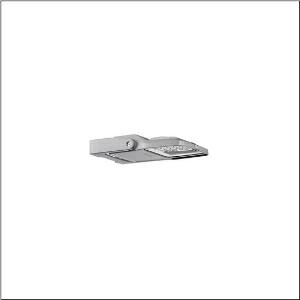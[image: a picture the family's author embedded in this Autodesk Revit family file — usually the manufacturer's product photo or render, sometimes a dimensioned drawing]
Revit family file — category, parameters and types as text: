
# Revit family: floodlight_fl_21_iq_micro___pl52_5xa7762a2d2a_5d06
name_source: partatom
category: Lighting Fixtures
units: mm (PartAtom-declared; Revit-internal decimal feet)

## family parameters
Cut with Voids When Loaded = No
Host = Face
Light Source = No
Part Type = Normal
Room Calculation Point = No
Round Connector Dimension = Use Diameter
Shared = No

## types (1)
- --- (1 x LED, 2890 lm, 23.1 W, 3000K)
    Apparent Load = 23 VA
    CIE Flux Codes = 26 60 98 100 100
    Color Rendering = 70
    Color Temperature = 3000K
    Default Elevation = 1800 mm
    Description = Floodlight FL 21 iQ micro, floodlight, primary light control with lens, of PMMA, primary optical cover: protective disc, of toughened safety glass, transparent, light distribution: PL52, light emission: direct distribution, installation type: surface-mounted, LED, High Power LED, rated luminous flux: 2.890lm, luminous efficacy: 125lm/W, light colour: 730, colour temperature: 3000K, control: Auto-Match, Temp-Guard, Night-Set, Smart-Wire, Desk-Remote (wireless, voltage-free reading and setting of iQ features in the workshop via application-optimized NFC function/RFID function), optimised constant luminous flux control (CLO 2.0), Street-Remote, with terminal, 6-pole, mains connection: 220..240V, AC, 50/60Hz, start of lifetime: 23W, end of service life: 24W, reduction: 11W, luminaire housing, of diecast aluminium, powder-coated, Siteco® metallic grey (DB 702S), corrosivity category C5 mid according to DIN EN ISO 12944, sealing non-destructively replaceable, design bracket, of diecast aluminium, powder-coated, Siteco® metallic grey (DB 702S), protection rating (complete): IP66, insulation class (complete): insulation class II (safety insulation), certification: CE, ENEC, VDE, protection symbol: D, impact resistance: IK07, permissible operating ambient temperature: -40..+40°C, permissible operating ambient temperature for outdoor applications: -40..+50°C, standard: DIN EN 12944, LABS conformity tested according to VDMA 24364:2018-05, packaging unit: 1 piece

Light Distribution: PL52
    Height = 65 mm
    Lamp = 1 x LED
    Lamp Light Flux = 2890 lm
    Lamp Power = 23.1 W
    Lamp count = 1
    Length = 312 mm
    Luminous efficacy = 125 lm/W
    Manufacturer = Siteco
    ModVariant = No
    Model = 5XA7762A2D2A
    Mounting Place = Wall
    Mounting Type = Surface mounted
    Number of Poles = 1
    OnlyDefault = Yes
    Power Factor = 1
    Product Name = Floodlight FL 21 iQ micro | PL52
    Product group = floodlight | wall mounted
    ProductGroupID = 2001
    Protection Class = Protection class II
    Protection Degree = IP 66
    RLX_Detail_Level = 1
    RLX_Emergency_Light_Flux = 0 lm
    RLX_Emergency_Type = 0
    RLX_Emergency_Type_DB = No
    RlxData = <blob elided: 97505 chars, md5=a6b8f968>
    Socket = socket
    Standby Power = 0 W
    System Light Flux = 2890 lm
    System Power = 23 W
    Type Comments = factory setting: luminous flux: 100 % | dim-lin: 254 | 455 mA
    Type Image = l_1006878.jpg
    URL = http://relux.com
    VarID = @adj_110669
    Voltage = 0 V
    Weight = 0.00 kg
    Width = 230 mm

## geometry (parser evidence)
native form markers: Blend x4, Sweep x14
no freeform markers — native parametric forms only
